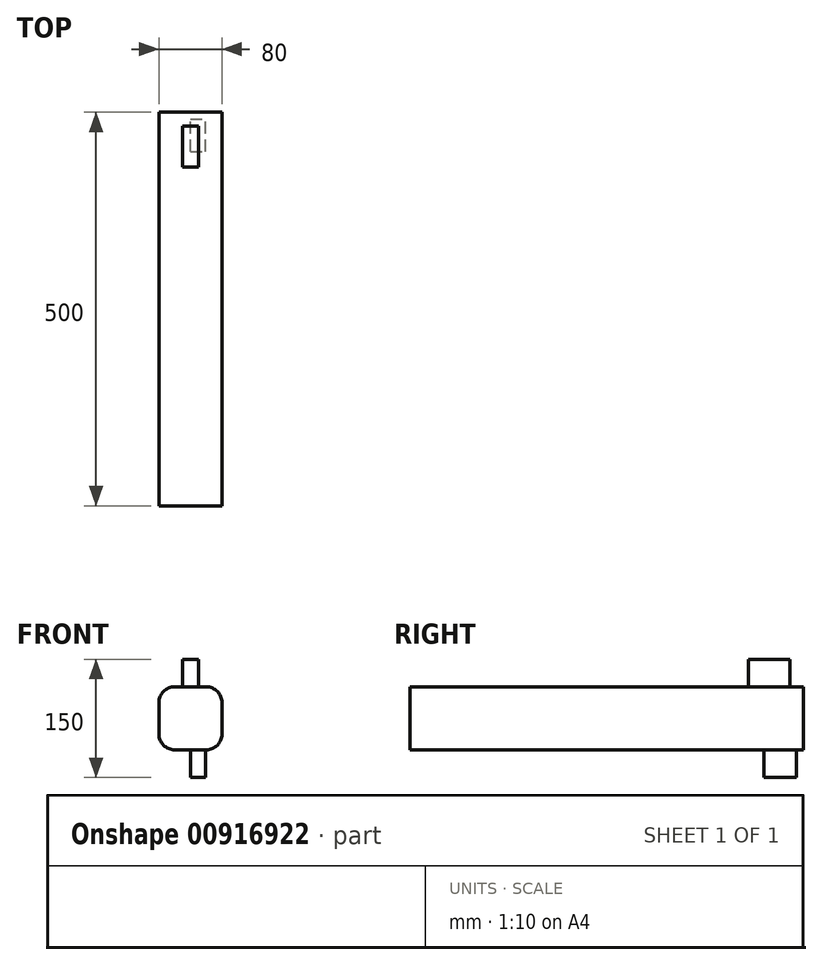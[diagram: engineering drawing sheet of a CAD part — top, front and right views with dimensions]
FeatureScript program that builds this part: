
annotation { "Feature Type Name" : "Feature", "Feature Type Description" : "" }
export const myFeature = defineFeature(function(context is Context, id is Id, definition is map)
    precondition{}
    {
        {
            var Q0;
            Q0=qCreatedBy(makeId("Top.planeOp"),FACE);
            var sketch = newSketch(context, id + "F0", { "sketchPlane" : qUnion([Q0])});
            skLineSegment(sketch, "E0.bottom", {"start": v(-40, -250) * mm, "end": v(40, -250) * mm});
            skLineSegment(sketch, "E0.top", {"start": v(-40, 250) * mm, "end": v(40, 250) * mm});
            skLineSegment(sketch, "E0.left", {"start": v(-40, -250) * mm, "end": v(-40, 250) * mm});
            skLineSegment(sketch, "E0.right", {"start": v(40, -250) * mm, "end": v(40, 250) * mm});
            skPoint(sketch, "E0.middle", {"position": v(0, 0) * mm});
            skSolve(sketch);
        }
        {
            var Q0;
            Q0=makeQuery(id+"F0.imprint","IMPRINT",FACE,{"disambiguationData":[TD([[makeQuery(id+"F0.imprint","IMPRINT",EDGE,{"derivedFrom":sQuery(id+"F0.wireOp",EDGE,"E0.bottom")}),1.0]])]});
            extrude(context, id + "F1", {"entities" : qUnion([Q0]), "depth" : 80 * mm, "offsetDistance" : 25 * mm});
        }
        {
            var Q0;
            Q0=makeQuery(id+"F1.opExtrude","CAP_EDGE",EDGE,{"disambiguationData":[OSD([sQuery(id+"F0.wireOp",EDGE,"E0.left")])],"isStart":true});
            var Q1;
            Q1=makeQuery(id+"F1.opExtrude","CAP_EDGE",EDGE,{"disambiguationData":[OSD([sQuery(id+"F0.wireOp",EDGE,"E0.right")])],"isStart":true});
            var Q2;
            Q2=makeQuery(id+"F1.opExtrude","CAP_EDGE",EDGE,{"disambiguationData":[OSD([sQuery(id+"F0.wireOp",EDGE,"E0.right")])],"isStart":false});
            var Q3;
            Q3=makeQuery(id+"F1.opExtrude","CAP_EDGE",EDGE,{"disambiguationData":[OSD([sQuery(id+"F0.wireOp",EDGE,"E0.left")])],"isStart":false});
            fillet(context, id + "F2", {"entities" : qUnion([Q0, Q1, Q2, Q3]), "radius" : 20 * mm, "tangentPropagation" : true, "allowEdgeOverflow" : false});
        }
        {
            var Q0;
            Q0=makeQuery(id+"F1.opExtrude","CAP_FACE",FACE,{"disambiguationData":[OSD([sQuery(id+"F0.wireOp",EDGE,"E0.bottom"),sQuery(id+"F0.wireOp",EDGE,"E0.top"),sQuery(id+"F0.wireOp",EDGE,"E0.left"),sQuery(id+"F0.wireOp",EDGE,"E0.right")])],"isStart":false});
            var sketch = newSketch(context, id + "F3", { "sketchPlane" : qUnion([Q0])});
            skLineSegment(sketch, "E1.bottom", {"start": v(10.08, 180.13) * mm, "end": v(-10.08, 180.13) * mm});
            skLineSegment(sketch, "E1.top", {"start": v(10.08, 232.66) * mm, "end": v(-10.08, 232.66) * mm});
            skLineSegment(sketch, "E1.left", {"start": v(10.08, 180.13) * mm, "end": v(10.08, 232.66) * mm});
            skLineSegment(sketch, "E1.right", {"start": v(-10.08, 180.13) * mm, "end": v(-10.08, 232.66) * mm});
            skPoint(sketch, "E1.middle", {"position": v(0, 206.4) * mm});
            skSolve(sketch);
        }
        {
            var Q0;
            Q0=makeQuery(id+"F3.imprint","IMPRINT",FACE,{"disambiguationData":[TD([[makeQuery(id+"F3.imprint","IMPRINT",EDGE,{"derivedFrom":sQuery(id+"F3.wireOp",EDGE,"E1.bottom")}),-1.0]])]});
            extrude(context, id + "F4", {"entities" : qUnion([Q0]), "operationType" : NewBodyOperationType.ADD, "depth" : 35 * mm, "offsetDistance" : 25 * mm});
        }
        {
            var Q0;
            Q0=makeQuery(id+"F1.opExtrude","CAP_FACE",FACE,{"disambiguationData":[OSD([sQuery(id+"F0.wireOp",EDGE,"E0.bottom"),sQuery(id+"F0.wireOp",EDGE,"E0.top"),sQuery(id+"F0.wireOp",EDGE,"E0.left"),sQuery(id+"F0.wireOp",EDGE,"E0.right")])],"isStart":true});
            var sketch = newSketch(context, id + "F5", { "sketchPlane" : qUnion([Q0])});
            skLineSegment(sketch, "E2.bottom", {"start": v(0, -200.07) * mm, "end": v(18.92, -200.07) * mm});
            skLineSegment(sketch, "E2.top", {"start": v(0, -241) * mm, "end": v(18.92, -241) * mm});
            skLineSegment(sketch, "E2.left", {"start": v(0, -200.07) * mm, "end": v(0, -241) * mm});
            skLineSegment(sketch, "E2.right", {"start": v(18.92, -200.07) * mm, "end": v(18.92, -241) * mm});
            skPoint(sketch, "E2.middle", {"position": v(9.46, -220.53) * mm});
            skPoint(sketch, "E2.cornerSnap0", {"position": v(0, -250) * mm});
            skSolve(sketch);
        }
        {
            var Q0;
            Q0=makeQuery(id+"F5.imprint","IMPRINT",FACE,{"disambiguationData":[TD([[makeQuery(id+"F5.imprint","IMPRINT",EDGE,{"derivedFrom":sQuery(id+"F5.wireOp",EDGE,"E2.bottom")}),-1.0]])]});
            extrude(context, id + "F6", {"entities" : qUnion([Q0]), "operationType" : NewBodyOperationType.ADD, "depth" : 35 * mm, "offsetDistance" : 25 * mm});
        }
    });
